# Revit family: 304_Cim776 HF-_
name_source: partatom
category: Pipe Accessories
revit_build: Autodesk Revit 2017 (Build: 20160225_1515(x64)
units: mm (PartAtom-declared; Revit-internal decimal feet)

## family parameters
Always vertical = Yes
Cut with Voids When Loaded = No
Part Type = Valve - Breaks Into
Round Connector Dimension = Use Diameter
Shared = No
Work Plane-Based = No

## types (6) — shared parameters
CAT0 = Yes
DD2 = 32 mm  [stored 0.104987 ft]
Description = AUTOMATIC BALANCING VALVE P.I.C.V. - PN 25 - "CR" BRASS - HIGH FLOW
HH3 = 20 mm  [stored 0.0656168 ft]
L2D_Min = 3048 mm
Manufacturer = Cimberio
QmdConnectorList = 301;D;302;D
URL = www.cimberio.it
magiPartTypeId = 304
magiProductFamilyId = Cim776 HF-*
zero-valued in all types: MC_Default_elevation

## per-type parameters (varying)
| type | CenSd_R1_6 | D | DD1 | DL | DL__ve | HH1 | L2D | LL1 | LL2 | LL5 | R1 | W2D | Y4 |
| Cim776 HF-15 | 12 mm  [stored 0.0393701 ft] | 15 mm | 22 mm | 12 mm  [stored 0.0393701 ft] | -12 mm | 60 mm | 96 mm | 48 mm  [stored 0.15748 ft] | 73 mm | 139 mm | 14 mm  [stored 0.0459318 ft] | 15 mm  [stored 0.0492126 ft] | 21 mm  [stored 0.0688976 ft] |
| Cim776 HF-50 | 29 mm | 50 mm | 54 mm | 19 mm | -19 mm | 63 mm | 155 mm | 78 mm | 118 mm | 210 mm | 34 mm  [stored 0.111549 ft] | 50 mm  [stored 0.164042 ft] | 60 mm |
| Cim776 HF-40 | 23 mm | 40 mm | 43 mm | 17 mm | -17 mm | 62 mm | 144 mm | 72 mm | 109 mm | 196 mm | 27 mm  [stored 0.0885827 ft] | 40 mm  [stored 0.131234 ft] | 56 mm  [stored 0.183727 ft] |
| Cim776 HF-32 | 21 mm  [stored 0.0688976 ft] | 32 mm | 39 mm | 15 mm  [stored 0.0492126 ft] | -15 mm | 56 mm  [stored 0.183727 ft] | 128 mm | 64 mm  [stored 0.209974 ft] | 97 mm | 142 mm | 25 mm  [stored 0.082021 ft] | 32 mm  [stored 0.104987 ft] | 45 mm |
| Cim776 HF-25 | 17 mm | 25 mm | 31 mm | 12 mm  [stored 0.0393701 ft] | -12 mm | 55 mm | 103 mm | 52 mm | 78 mm | 134 mm | 20 mm  [stored 0.0656168 ft] | 25 mm  [stored 0.082021 ft] | 35 mm  [stored 0.114829 ft] |
| Cim776 HF-20 | 14 mm  [stored 0.0459318 ft] | 20 mm | 26 mm | 12 mm  [stored 0.0393701 ft] | -12 mm | 58 mm | 97 mm | 49 mm | 74 mm | 136 mm | 16 mm  [stored 0.0524934 ft] | 20 mm  [stored 0.0656168 ft] | 28 mm  [stored 0.0918635 ft] |

note: column(s) folded — value = type name in every type: magiProductCode, magiProductId

note: [stored X ft] marks values corroborated as IEEE doubles in the binary element streams (Revit-internal decimal feet)

## geometry (parser evidence)
native form markers: Sweep x2
no freeform markers — native parametric forms only
